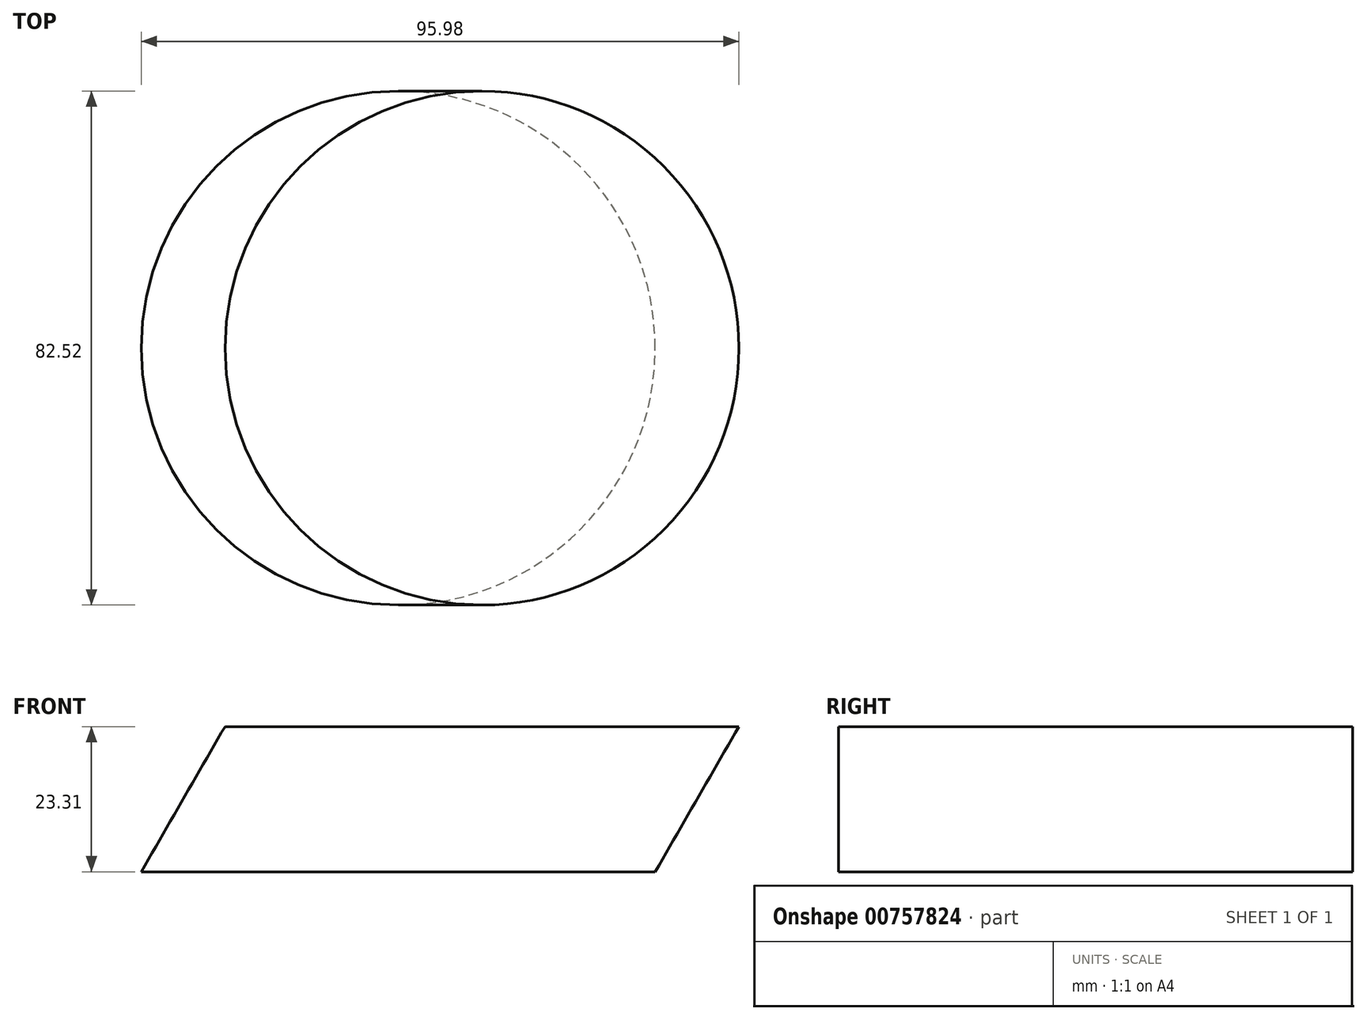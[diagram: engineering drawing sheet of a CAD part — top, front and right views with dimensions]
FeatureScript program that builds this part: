
annotation { "Feature Type Name" : "Feature", "Feature Type Description" : "" }
export const myFeature = defineFeature(function(context is Context, id is Id, definition is map)
    precondition{}
    {
        {
            var Q0;
            Q0=qCreatedBy(makeId("Top.planeOp"),FACE);
            var sketch = newSketch(context, id + "F0", { "sketchPlane" : qUnion([Q0])});
            skCircle(sketch, "E0", {"center": v(0, 0) * mm, "radius": 41.26 * mm});
            skSolve(sketch);
        }
        {
            var Q0;
            Q0=qCreatedBy(makeId("Front.planeOp"),FACE);
            var sketch = newSketch(context, id + "F1", { "sketchPlane" : qUnion([Q0])});
            skLineSegment(sketch, "E1", {"start": v(13.46, 23.31) * mm, "end": v(0, 0) * mm});
            skSolve(sketch);
        }
        {
            var Q0;
            Q0=makeQuery(id+"F0.imprint","IMPRINT",FACE,{"disambiguationData":[TD([[makeQuery(id+"F0.imprint","IMPRINT",EDGE,{"derivedFrom":sQuery(id+"F0.wireOp",EDGE,"E0")}),1.0]])]});
            var Q1;
            Q1=sQuery(id+"F1.wireOp",EDGE,"E1");
            sweep(context, id + "F2", {"profiles" : qUnion([Q0]), "path" : qUnion([Q1])});
        }
    });
